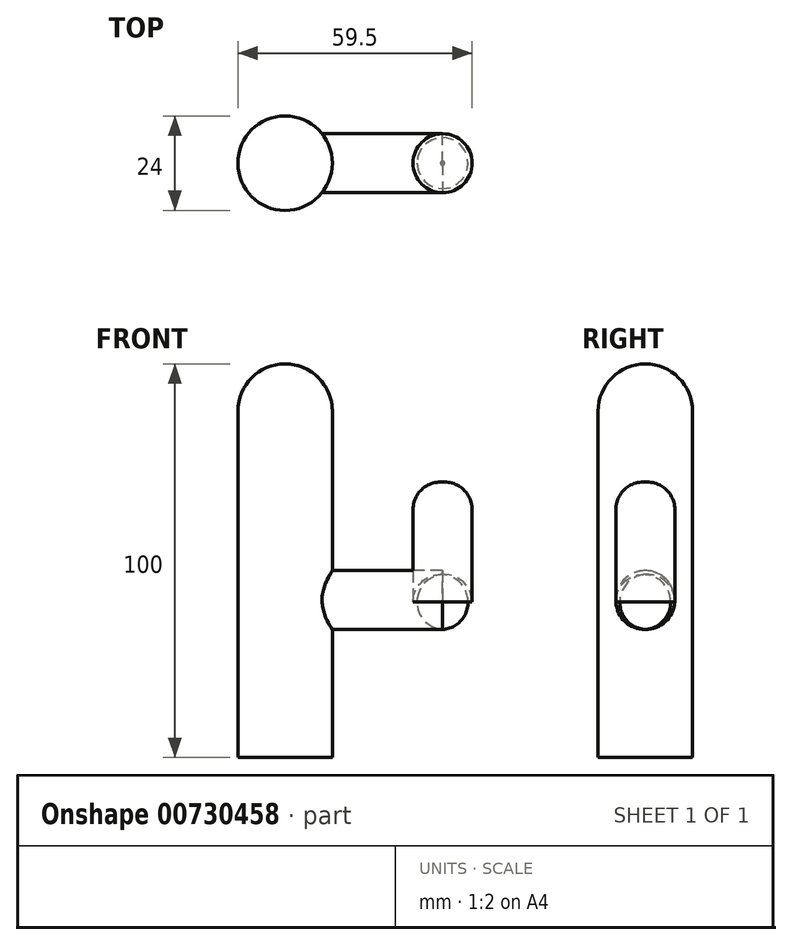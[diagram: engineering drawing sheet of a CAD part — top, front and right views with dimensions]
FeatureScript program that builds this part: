
annotation { "Feature Type Name" : "Feature", "Feature Type Description" : "" }
export const myFeature = defineFeature(function(context is Context, id is Id, definition is map)
    precondition{}
    {
        {
            var Q0;
            Q0=qCreatedBy(makeId("Top.planeOp"),FACE);
            var sketch = newSketch(context, id + "F0", { "sketchPlane" : qUnion([Q0])});
            skCircle(sketch, "E0", {"center": v(0, 0) * mm, "radius": 12 * mm});
            skSolve(sketch);
        }
        {
            var Q0;
            Q0=makeQuery(id+"F0.imprint","IMPRINT",FACE,{"disambiguationData":[TD([[makeQuery(id+"F0.imprint","IMPRINT",EDGE,{"derivedFrom":sQuery(id+"F0.wireOp",EDGE,"E0")}),1.0]])]});
            extrude(context, id + "F1", {"entities" : qUnion([Q0]), "depth" : 100 * mm, "offsetDistance" : 25 * mm});
        }
        {
            var Q0;
            Q0=makeQuery(id+"F1.opExtrude","CAP_EDGE",EDGE,{"disambiguationData":[OSD([sQuery(id+"F0.wireOp",EDGE,"E0")])],"isStart":false});
            fillet(context, id + "F2", {"entities" : qUnion([Q0]), "radius" : 12 * mm, "tangentPropagation" : true, "allowEdgeOverflow" : false});
        }
        {
            var Q0;
            Q0=qCreatedBy(makeId("Right.planeOp"),FACE);
            var sketch = newSketch(context, id + "F3", { "sketchPlane" : qUnion([Q0])});
            skCircle(sketch, "E1", {"center": v(0, 40) * mm, "radius": 7.5 * mm});
            skSolve(sketch);
        }
        {
            var Q0;
            Q0 = qSketchRegion(id + "F3", true);
            extrude(context, id + "F4", {"entities" : qUnion([Q0]), "operationType" : NewBodyOperationType.ADD, "depth" : 40 * mm, "offsetDistance" : 25 * mm});
        }
        {
            var Q0;
            Q0=qCreatedBy(makeId("Top.planeOp"),FACE);
            var sketch = newSketch(context, id + "F5", { "sketchPlane" : qUnion([Q0])});
            skCircle(sketch, "E2", {"center": v(40, 0) * mm, "radius": 7.5 * mm});
            skSolve(sketch);
        }
        {
            var Q0;
            Q0=makeQuery(id+"F5.imprint","IMPRINT",FACE,{"disambiguationData":[TD([[makeQuery(id+"F5.imprint","IMPRINT",EDGE,{"derivedFrom":sQuery(id+"F5.wireOp",EDGE,"E2")}),1.0]])]});
            extrude(context, id + "F6", {"entities" : qUnion([Q0]), "depth" : 70 * mm, "offsetDistance" : 25 * mm, "hasSecondDirection" : true, "secondDirectionOppositeDirection" : false, "secondDirectionDepth" : (40 - 7.5) * mm});
        }
        {
            var Q0;
            Q0=makeQuery(id+"F6.opExtrude","CAP_EDGE",EDGE,{"disambiguationData":[OSD([sQuery(id+"F5.wireOp",EDGE,"E2")])],"isStart":true});
            fillet(context, id + "F7", {"entities" : qUnion([Q0]), "radius" : 7 * mm, "tangentPropagation" : true, "allowEdgeOverflow" : false});
        }
        {
            var Q0;
            Q0=makeQuery(id+"F6.opExtrude","CAP_EDGE",EDGE,{"disambiguationData":[OSD([sQuery(id+"F5.wireOp",EDGE,"E2")])],"isStart":false});
            fillet(context, id + "F8", {"entities" : qUnion([Q0]), "radius" : 7 * mm, "tangentPropagation" : true, "allowEdgeOverflow" : false});
        }
    });
